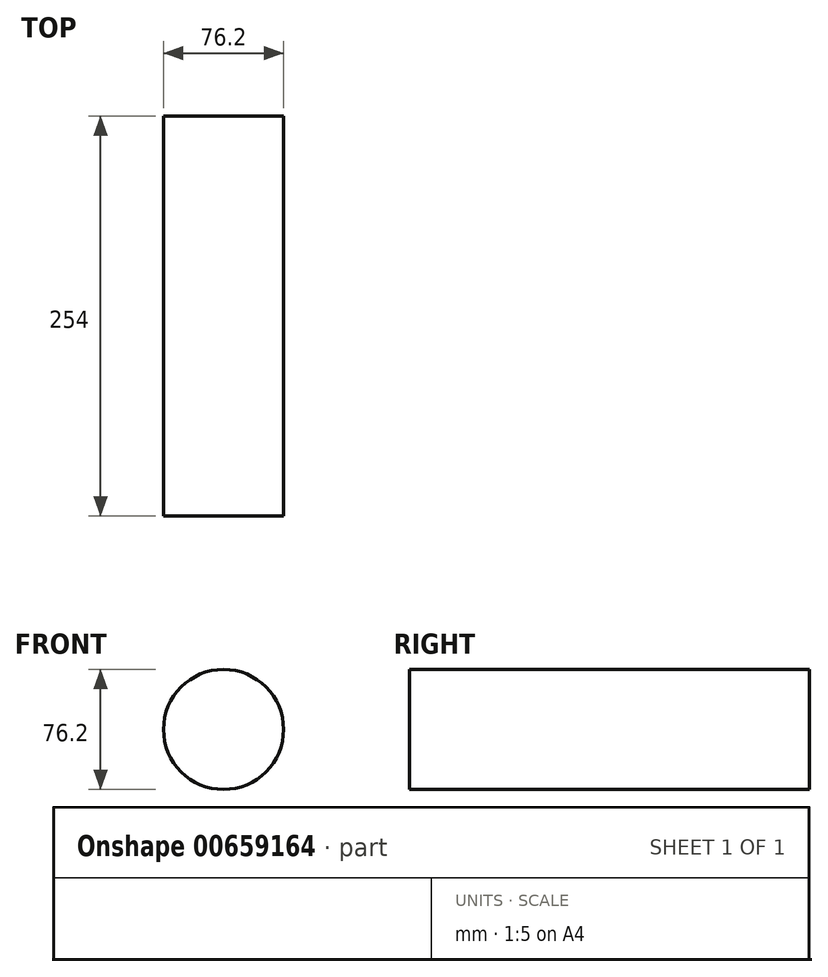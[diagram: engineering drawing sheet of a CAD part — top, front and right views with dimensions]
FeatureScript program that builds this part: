
annotation { "Feature Type Name" : "Feature", "Feature Type Description" : "" }
export const myFeature = defineFeature(function(context is Context, id is Id, definition is map)
    precondition{}
    {
        {
            var Q0;
            Q0=qCreatedBy(makeId("Front.planeOp"),FACE);
            var sketch = newSketch(context, id + "F0", { "sketchPlane" : qUnion([Q0])});
            skCircle(sketch, "E0", {"center": v(0, 0) * mm, "radius": 38.1 * mm});
            skSolve(sketch);
        }
        {
            var Q0;
            Q0 = qSketchRegion(id + "F0", true);
            extrude(context, id + "F1", {"entities" : qUnion([Q0]), "depth" : 254 * mm, "offsetDistance" : 25.4 * mm});
        }
    });
